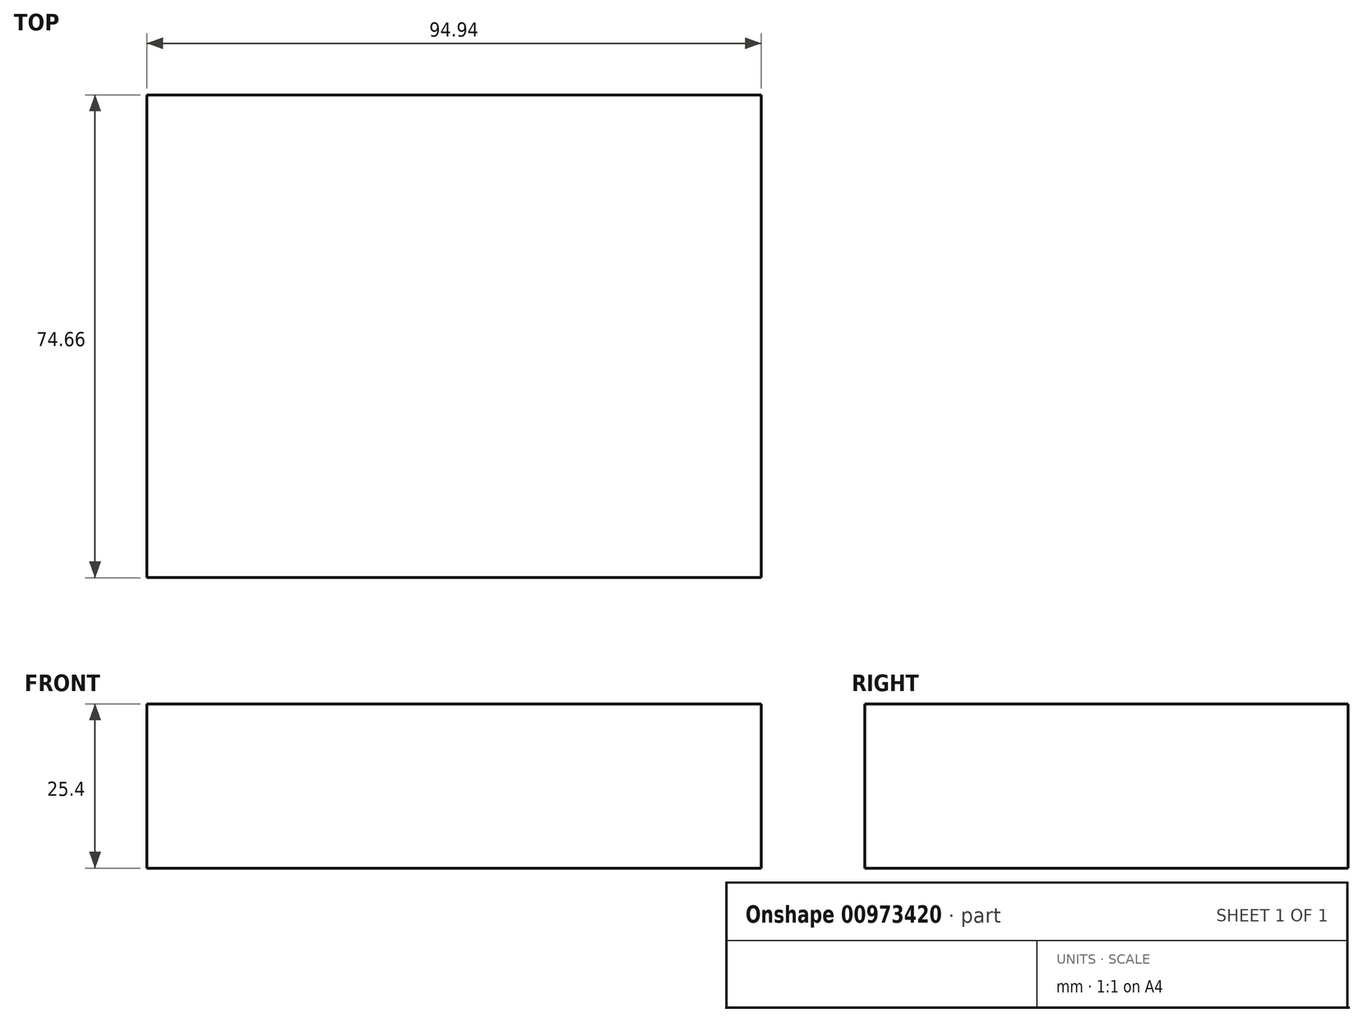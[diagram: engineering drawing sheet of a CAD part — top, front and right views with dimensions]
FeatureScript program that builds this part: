
annotation { "Feature Type Name" : "Feature", "Feature Type Description" : "" }
export const myFeature = defineFeature(function(context is Context, id is Id, definition is map)
    precondition{}
    {
        {
            var Q0;
            Q0=qCreatedBy(makeId("Top.planeOp"),FACE);
            var sketch = newSketch(context, id + "F0", { "sketchPlane" : qUnion([Q0])});
            skLineSegment(sketch, "E0.bottom", {"start": v(-37.6, 37.67) * mm, "end": v(57.35, 37.67) * mm});
            skLineSegment(sketch, "E0.top", {"start": v(-37.6, -36.99) * mm, "end": v(57.35, -36.99) * mm});
            skLineSegment(sketch, "E0.left", {"start": v(-37.6, 37.67) * mm, "end": v(-37.6, -36.99) * mm});
            skLineSegment(sketch, "E0.right", {"start": v(57.35, 37.67) * mm, "end": v(57.35, -36.99) * mm});
            skLineSegment(sketch, "E1.bottom", {"start": v(29.9, 37.67) * mm, "end": v(9.88, 37.67) * mm});
            skLineSegment(sketch, "E1.top", {"start": v(29.9, -36.99) * mm, "end": v(9.88, -36.99) * mm});
            skLineSegment(sketch, "E1.left", {"start": v(29.9, 37.67) * mm, "end": v(29.9, -36.99) * mm});
            skLineSegment(sketch, "E1.right", {"start": v(9.88, 37.67) * mm, "end": v(9.88, -36.99) * mm});
            skSolve(sketch);
        }
        {
            var Q0;
            {var subQ2=sQuery(id+"F0.wireOp",EDGE,"E0.right");Q0=makeQuery(id+"F0.imprint","IMPRINT",FACE,{"disambiguationData":[TD([[makeQuery(id+"F0.imprint","IMPRINT",EDGE,{"derivedFrom":subQ2}),-1.0]])]});}
            var Q1;
            {var subQ0=sQuery(id+"F0.wireOp",EDGE,"E1.left");Q1=makeQuery(id+"F0.imprint","IMPRINT",FACE,{"disambiguationData":[TD([[makeQuery(id+"F0.imprint","IMPRINT",EDGE,{"derivedFrom":subQ0}),-1.0]])]});}
            var Q2;
            {var subQ0=sQuery(id+"F0.wireOp",EDGE,"E0.left");Q2=makeQuery(id+"F0.imprint","IMPRINT",FACE,{"disambiguationData":[TD([[makeQuery(id+"F0.imprint","IMPRINT",EDGE,{"derivedFrom":subQ0}),1.0]])]});}
            extrude(context, id + "F1", {"entities" : qUnion([Q0, Q1, Q2]), "depth" : 25.4 * mm, "offsetDistance" : 25.4 * mm});
        }
        {
            var Q0;
            Q0=makeQuery(id+"F1.opExtrude","SWEPT_FACE",FACE,{"disambiguationData":[OSD([sQuery(id+"F0.wireOp",EDGE,"E0.top")])]});
            cPlane(context, id + "F2", {"entities" : qUnion([Q0]), "cplaneType" : CPlaneType.OFFSET, "offset" : 25.4 * mm, "width" : 152.4 * mm, "height" : 152.4 * mm});
        }
    });
